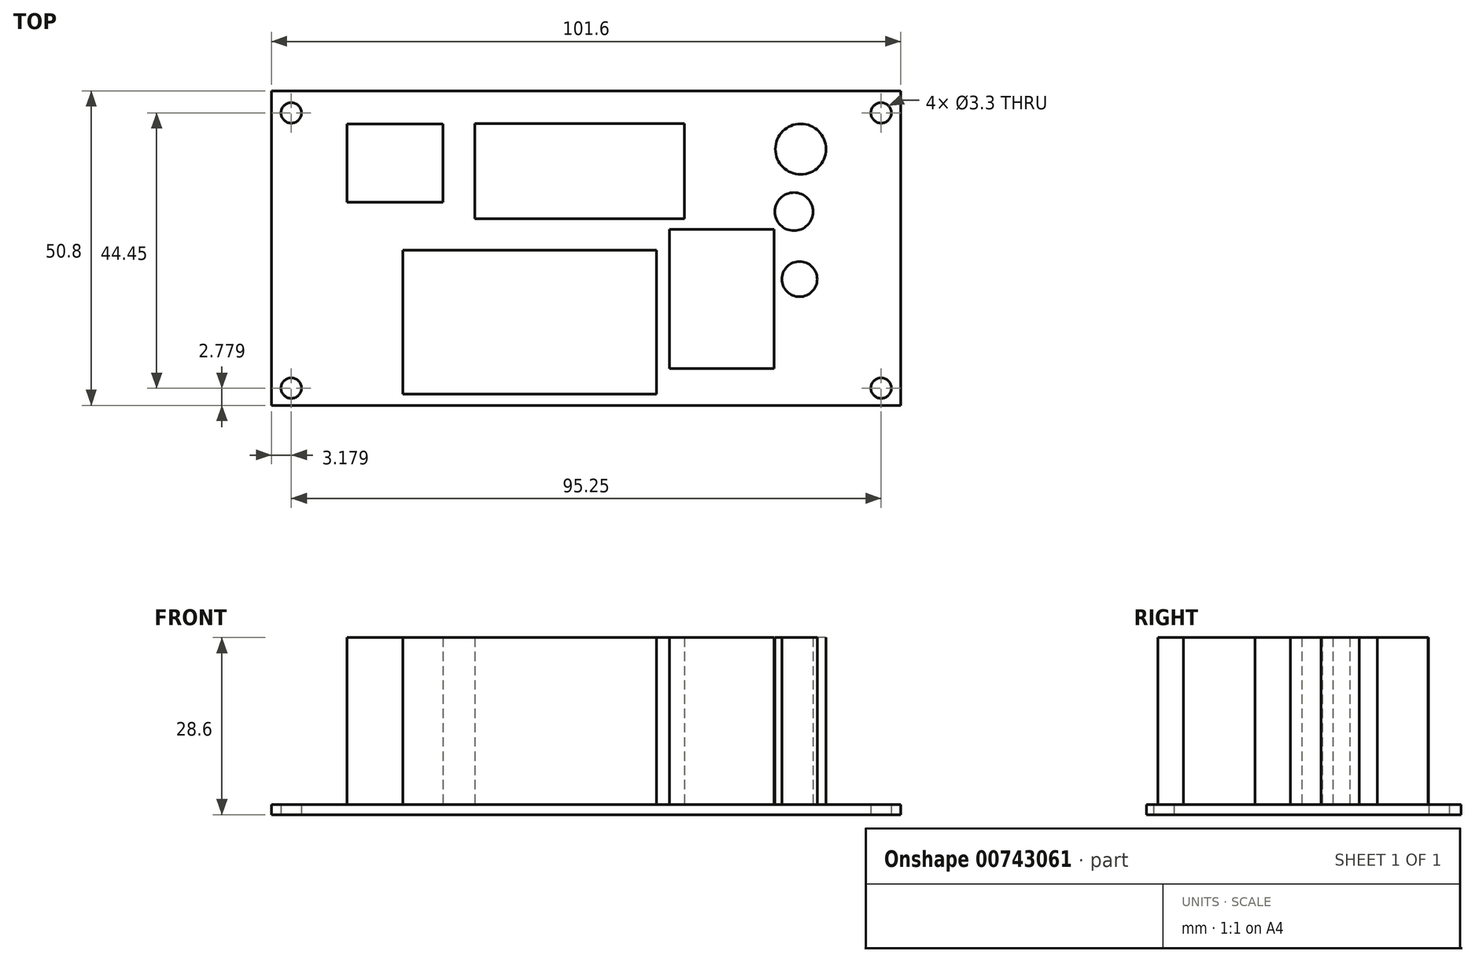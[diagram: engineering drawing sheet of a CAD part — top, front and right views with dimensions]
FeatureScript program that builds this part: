
annotation { "Feature Type Name" : "Feature", "Feature Type Description" : "" }
export const myFeature = defineFeature(function(context is Context, id is Id, definition is map)
    precondition{}
    {
        {
            var Q0;
            Q0=qCreatedBy(makeId("Top.planeOp"),FACE);
            var sketch = newSketch(context, id + "F0", { "sketchPlane" : qUnion([Q0])});
            skLineSegment(sketch, "E0.bottom", {"start": v(-69.98, 27.13) * mm, "end": v(31.62, 27.13) * mm});
            skLineSegment(sketch, "E0.top", {"start": v(-69.98, -23.67) * mm, "end": v(31.62, -23.67) * mm});
            skLineSegment(sketch, "E0.left", {"start": v(-69.98, 27.13) * mm, "end": v(-69.98, -23.67) * mm});
            skLineSegment(sketch, "E0.right", {"start": v(31.62, 27.13) * mm, "end": v(31.62, -23.67) * mm});
            skLineSegment(sketch, "E1", {"start": v(-66.8, 27.13) * mm, "end": v(-66.8, -23.67) * mm, "construction": true});
            skLineSegment(sketch, "E2", {"start": v(28.45, 27.13) * mm, "end": v(28.45, -23.67) * mm, "construction": true});
            skCircle(sketch, "E3", {"center": v(-66.8, 23.56) * mm, "radius": 1.65 * mm});
            skCircle(sketch, "E4", {"center": v(-66.8, -20.9) * mm, "radius": 1.65 * mm});
            skLineSegment(sketch, "E5", {"start": v(-66.8, -20.9) * mm, "end": v(28.45, -20.9) * mm, "construction": true});
            skCircle(sketch, "E6", {"center": v(28.45, -20.9) * mm, "radius": 1.65 * mm});
            skLineSegment(sketch, "E7", {"start": v(-66.8, 23.56) * mm, "end": v(28.45, 23.56) * mm, "construction": true});
            skCircle(sketch, "E8", {"center": v(28.45, 23.56) * mm, "radius": 1.65 * mm});
            skSolve(sketch);
        }
        {
            var Q0;
            Q0=makeQuery(id+"F0.imprint","IMPRINT",FACE,{"disambiguationData":[TD([[makeQuery(id+"F0.imprint","IMPRINT",EDGE,{"derivedFrom":sQuery(id+"F0.wireOp",EDGE,"E0.bottom")}),-1.0]])]});
            extrude(context, id + "F1", {"entities" : qUnion([Q0]), "depth" : 1.6 * mm, "offsetDistance" : 25 * mm});
        }
        {
            var Q0;
            Q0=makeQuery(id+"F1.opExtrude","CAP_FACE",FACE,{"disambiguationData":[OSD([sQuery(id+"F0.wireOp",EDGE,"E0.bottom"),sQuery(id+"F0.wireOp",EDGE,"E0.top"),sQuery(id+"F0.wireOp",EDGE,"E0.left"),sQuery(id+"F0.wireOp",EDGE,"E0.right"),sQuery(id+"F0.wireOp",EDGE,"E3"),sQuery(id+"F0.wireOp",EDGE,"E4"),sQuery(id+"F0.wireOp",EDGE,"E6"),sQuery(id+"F0.wireOp",EDGE,"E8")])],"isStart":false});
            var sketch = newSketch(context, id + "F2", { "sketchPlane" : qUnion([Q0])});
            skLineSegment(sketch, "E9.bottom", {"start": v(-57.81, 21.77) * mm, "end": v(-42.31, 21.77) * mm});
            skLineSegment(sketch, "E9.top", {"start": v(-57.81, 9.15) * mm, "end": v(-42.31, 9.15) * mm});
            skLineSegment(sketch, "E9.left", {"start": v(-57.81, 21.77) * mm, "end": v(-57.81, 9.15) * mm});
            skLineSegment(sketch, "E9.right", {"start": v(-42.31, 21.77) * mm, "end": v(-42.31, 9.15) * mm});
            skLineSegment(sketch, "E10.bottom", {"start": v(-37.17, 21.86) * mm, "end": v(-3.29, 21.86) * mm});
            skLineSegment(sketch, "E10.top", {"start": v(-37.17, 6.45) * mm, "end": v(-3.29, 6.45) * mm});
            skLineSegment(sketch, "E10.left", {"start": v(-37.17, 21.86) * mm, "end": v(-37.17, 6.45) * mm});
            skLineSegment(sketch, "E10.right", {"start": v(-3.29, 21.86) * mm, "end": v(-3.29, 6.45) * mm});
            skLineSegment(sketch, "E11.bottom", {"start": v(-48.8, 1.4) * mm, "end": v(-7.8, 1.4) * mm});
            skLineSegment(sketch, "E11.top", {"start": v(-48.8, -21.85) * mm, "end": v(-7.8, -21.85) * mm});
            skLineSegment(sketch, "E11.left", {"start": v(-48.8, 1.4) * mm, "end": v(-48.8, -21.85) * mm});
            skLineSegment(sketch, "E11.right", {"start": v(-7.8, 1.4) * mm, "end": v(-7.8, -21.85) * mm});
            skLineSegment(sketch, "E12.bottom", {"start": v(-5.72, 4.74) * mm, "end": v(11.13, 4.74) * mm});
            skLineSegment(sketch, "E12.top", {"start": v(-5.72, -17.7) * mm, "end": v(11.13, -17.7) * mm});
            skLineSegment(sketch, "E12.left", {"start": v(-5.72, 4.74) * mm, "end": v(-5.72, -17.7) * mm});
            skLineSegment(sketch, "E12.right", {"start": v(11.13, 4.74) * mm, "end": v(11.13, -17.7) * mm});
            skCircle(sketch, "E13", {"center": v(15.46, 17.71) * mm, "radius": 4.09 * mm});
            skCircle(sketch, "E14", {"center": v(14.38, 7.62) * mm, "radius": 3.08 * mm});
            skCircle(sketch, "E15", {"center": v(15.28, -3.28) * mm, "radius": 2.85 * mm});
            skSolve(sketch);
        }
        {
            var Q0;
            Q0 = qSketchRegion(id + "F2", true);
            extrude(context, id + "F3", {"entities" : qUnion([Q0]), "operationType" : NewBodyOperationType.ADD, "depth" : 27 * mm, "offsetDistance" : 25 * mm});
        }
    });
